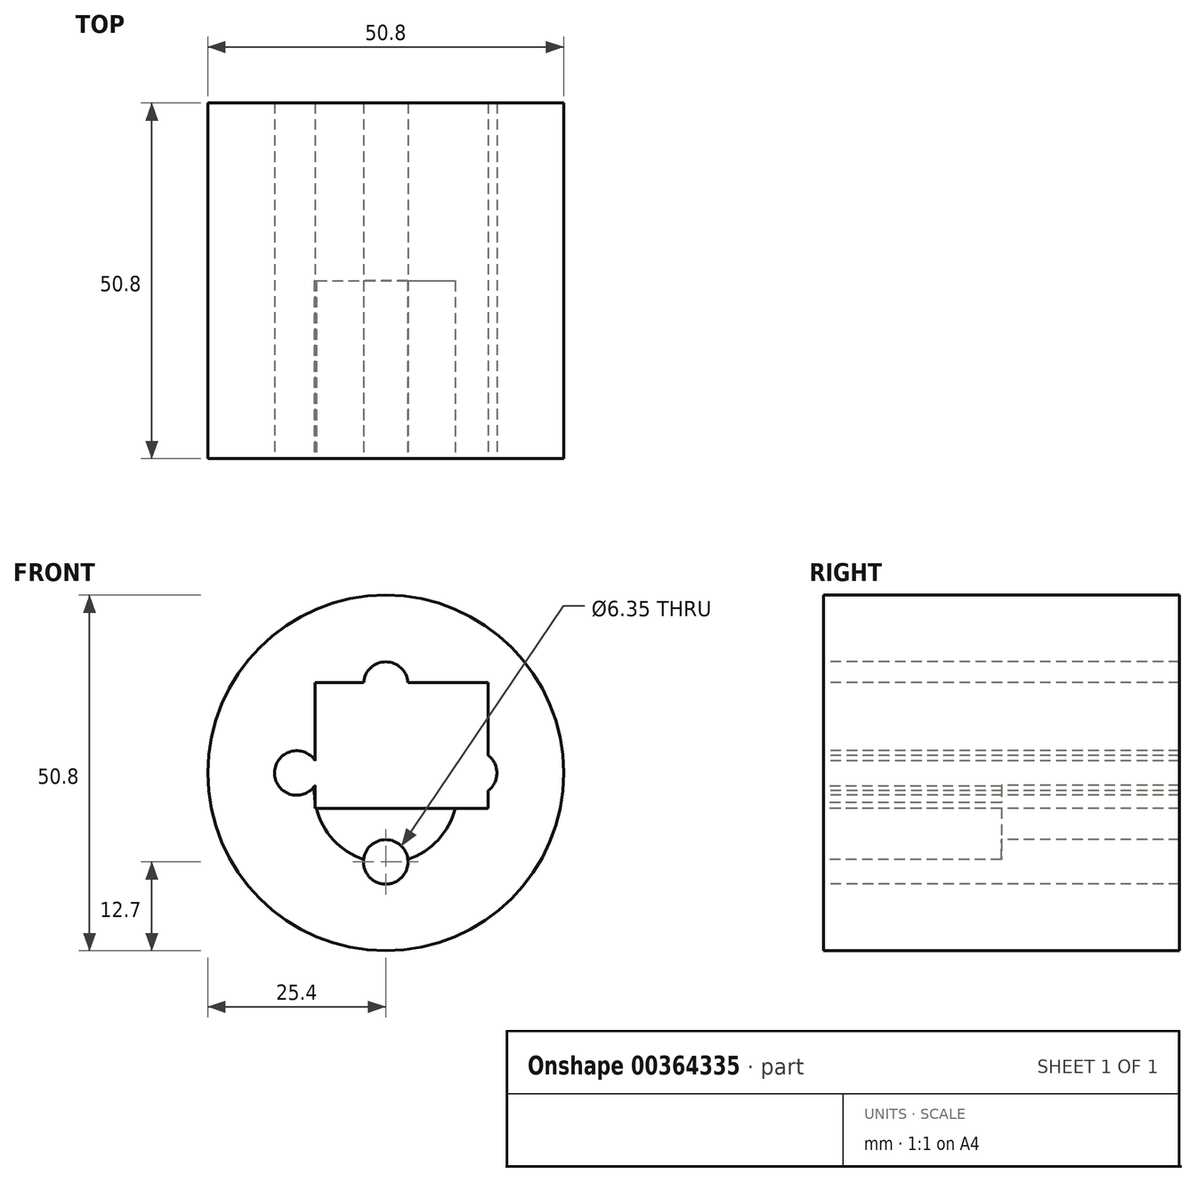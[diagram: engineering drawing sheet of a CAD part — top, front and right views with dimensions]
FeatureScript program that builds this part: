
annotation { "Feature Type Name" : "Feature", "Feature Type Description" : "" }
export const myFeature = defineFeature(function(context is Context, id is Id, definition is map)
    precondition{}
    {
        {
            var Q0;
            Q0=qCreatedBy(makeId("Front.planeOp"),FACE);
            var sketch = newSketch(context, id + "F0", { "sketchPlane" : qUnion([Q0])});
            skCircle(sketch, "E0", {"center": v(0, 0) * mm, "radius": 25.4 * mm});
            skSolve(sketch);
        }
        {
            var Q0;
            Q0 = qSketchRegion(id + "F0", true);
            extrude(context, id + "F1", {"entities" : qUnion([Q0]), "depth" : 50.8 * mm});
        }
        {
            var Q0;
            Q0=makeQuery(id+"F1.opExtrude","CAP_FACE",FACE,{"disambiguationData":[OSD([sQuery(id+"F0.wireOp",EDGE,"E0")])],"isStart":false});
            var sketch = newSketch(context, id + "F2", { "sketchPlane" : qUnion([Q0])});
            skCircle(sketch, "E1", {"center": v(0, 12.7) * mm, "radius": 3.18 * mm});
            skCircle(sketch, "E2.1.0", {"center": v(12.7, 0) * mm, "radius": 3.18 * mm});
            skCircle(sketch, "E2.2.0", {"center": v(0, -12.7) * mm, "radius": 3.18 * mm});
            skCircle(sketch, "E2.3.0", {"center": v(-12.7, 0) * mm, "radius": 3.18 * mm});
            skPoint(sketch, "E2.center", {"position": v(0, 0) * mm});
            skLineSegment(sketch, "E2.anchor1", {"start": v(0, 0) * mm, "end": v(0, 12.7) * mm, "construction": true});
            skLineSegment(sketch, "E2.anchor2", {"start": v(0, 0) * mm, "end": v(-12.7, 0) * mm, "construction": true});
            skSolve(sketch);
        }
        {
            var Q0;
            Q0 = qSketchRegion(id + "F2", true);
            extrude(context, id + "F3", {"entities" : qUnion([Q0]), "operationType" : NewBodyOperationType.REMOVE, "endBound" : BoundingType.UP_TO_NEXT, "oppositeDirection" : true, "depth" : 25.4 * mm});
        }
        {
            var Q0;
            Q0=makeQuery(id+"F1.opExtrude","CAP_FACE",FACE,{"disambiguationData":[OSD([sQuery(id+"F0.wireOp",EDGE,"E0")])],"isStart":false});
            var sketch = newSketch(context, id + "F4", { "sketchPlane" : qUnion([Q0])});
            skCircle(sketch, "E3", {"center": v(0, -2.65) * mm, "radius": 10.18 * mm});
            skSolve(sketch);
        }
        {
            var Q0;
            Q0 = qSketchRegion(id + "F4", true);
            extrude(context, id + "F5", {"entities" : qUnion([Q0]), "operationType" : NewBodyOperationType.REMOVE, "oppositeDirection" : true, "depth" : 25.4 * mm});
        }
        {
            var Q0;
            Q0=makeQuery(id+"F1.opExtrude","CAP_FACE",FACE,{"disambiguationData":[OSD([sQuery(id+"F0.wireOp",EDGE,"E0")])],"isStart":false});
            var sketch = newSketch(context, id + "F6", { "sketchPlane" : qUnion([Q0])});
            skLineSegment(sketch, "E4.bottom", {"start": v(-10.06, 12.94) * mm, "end": v(14.64, 12.94) * mm});
            skLineSegment(sketch, "E4.top", {"start": v(-10.06, -5.04) * mm, "end": v(14.64, -5.04) * mm});
            skLineSegment(sketch, "E4.left", {"start": v(-10.06, 12.94) * mm, "end": v(-10.06, -5.04) * mm});
            skLineSegment(sketch, "E4.right", {"start": v(14.64, 12.94) * mm, "end": v(14.64, -5.04) * mm});
            skSolve(sketch);
        }
        {
            var Q0;
            Q0 = qSketchRegion(id + "F6", true);
            extrude(context, id + "F7", {"entities" : qUnion([Q0]), "operationType" : NewBodyOperationType.REMOVE, "oppositeDirection" : true, "depth" : 50.8 * mm});
        }
    });
